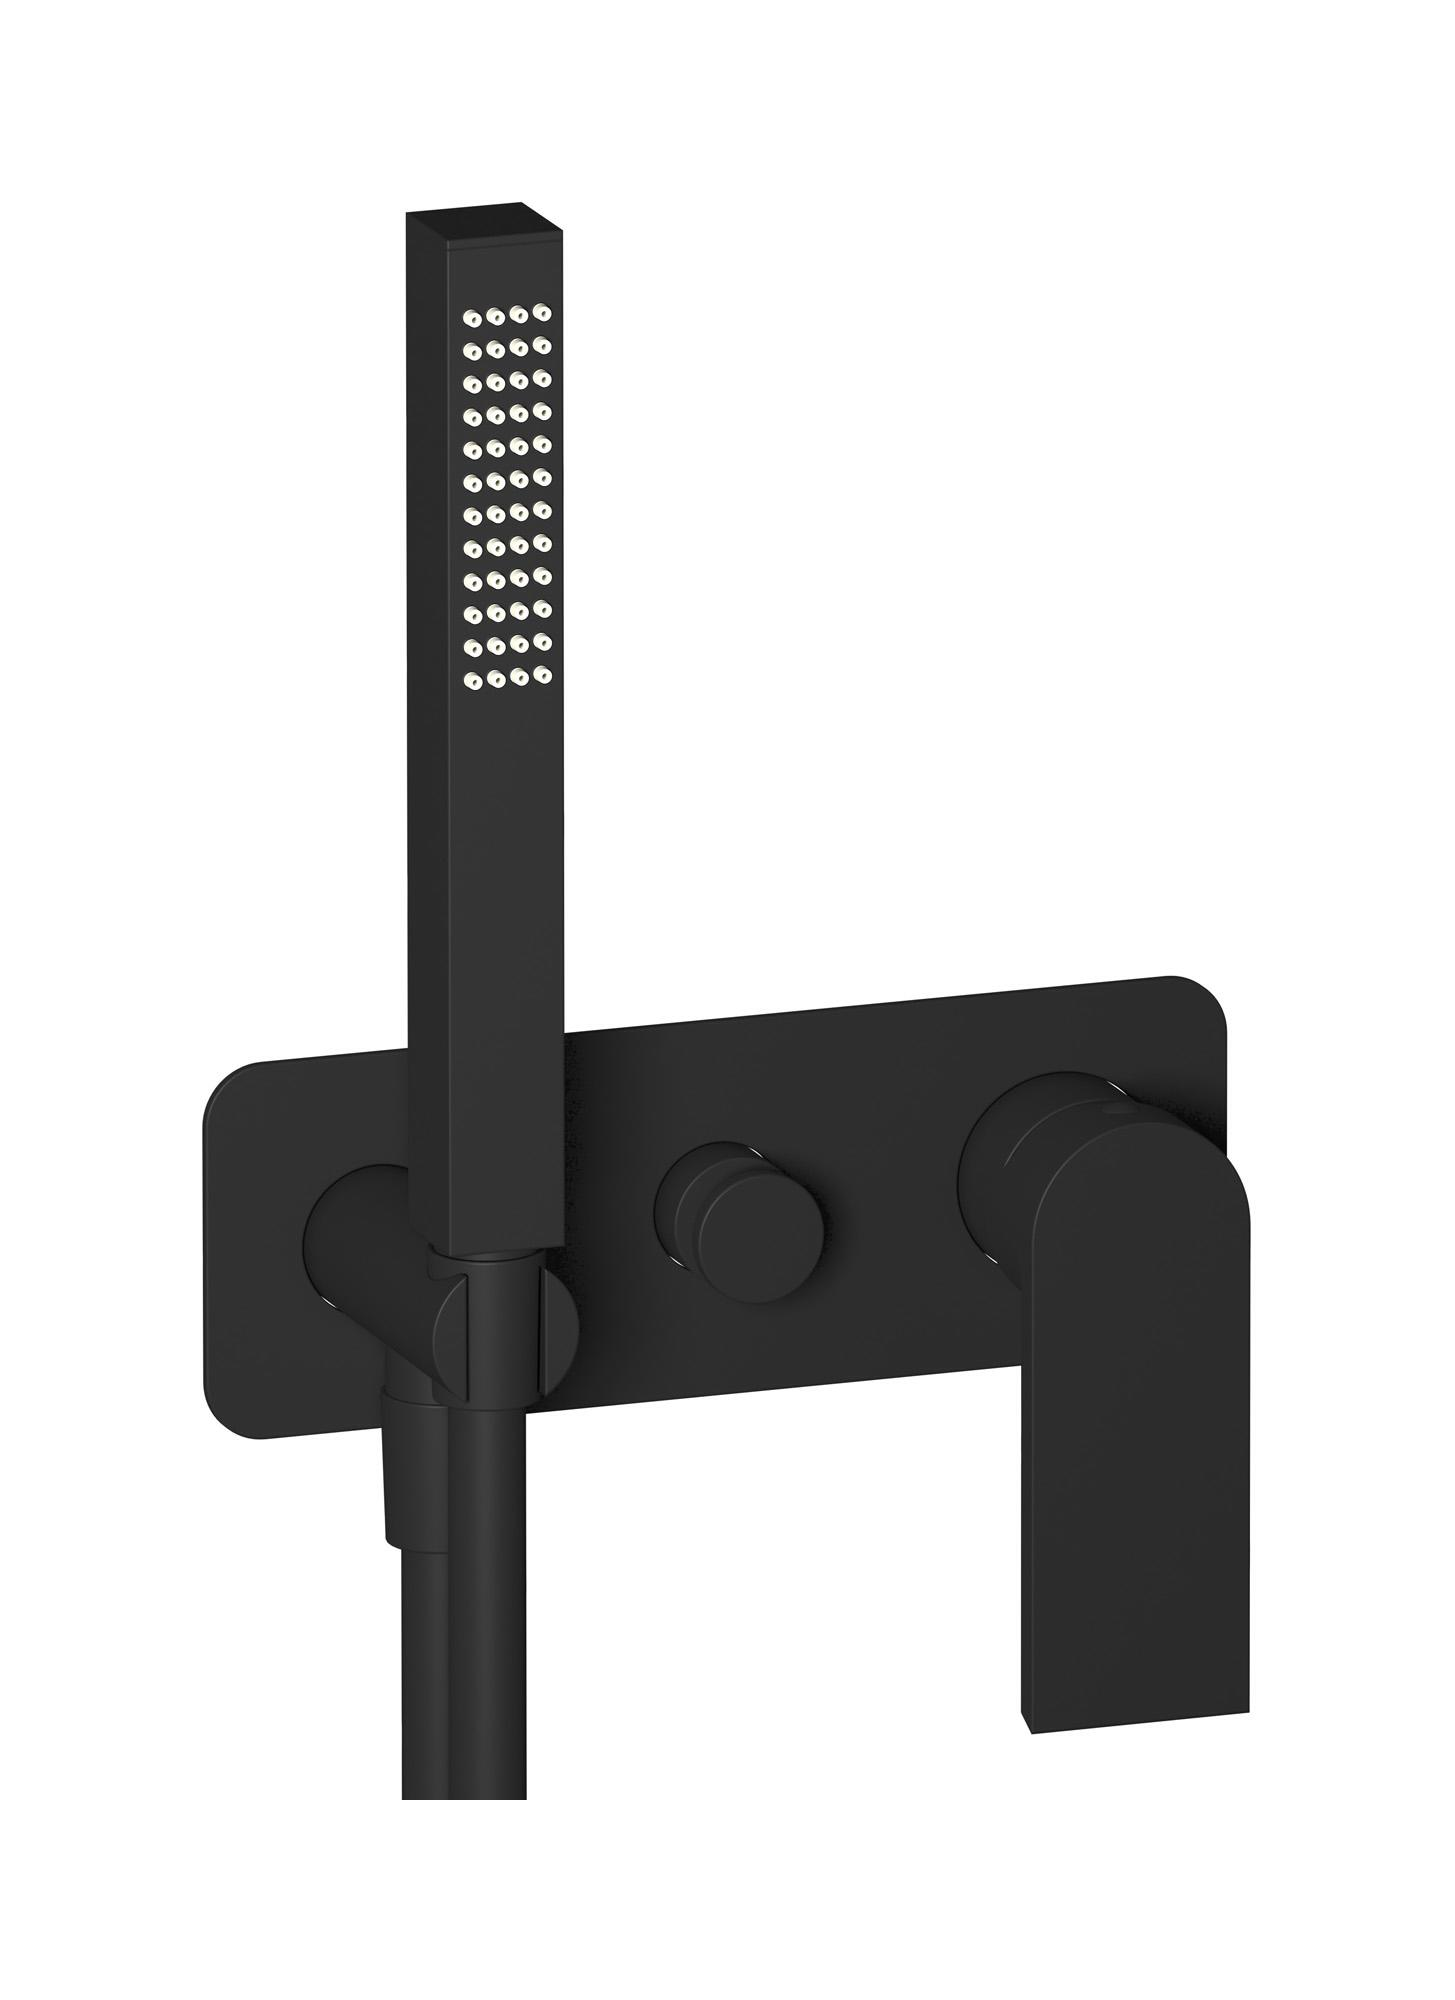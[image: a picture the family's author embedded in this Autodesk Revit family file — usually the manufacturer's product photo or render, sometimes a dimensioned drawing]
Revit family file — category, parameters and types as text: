
# Revit family: K3313
name_source: partatom
category: Apparecchi idraulici
units: mm (PartAtom-declared; Revit-internal decimal feet)

## family parameters
Basato su piano di lavoro = No
Condiviso = No
Mantieni orientamento annotazione = No
Numero OmniClass = 23.45.55.17
Punto di calcolo locali = No
Quota connettore circolare = Usa diametro
Sempre verticale = Sì
Taglio con vuoti quando caricato = No
Tipo di parte = Normale
Titolo OmniClass = Mixing Faucets

## types (8) — shared parameters
Cold water inlet = 10 mm  [stored 0.0328084 ft]
Commenti sul tipo = Wall mixer
Connessione CW = No
Connessione HW = No
Connessione di scarico = No
Connessione di ventilazione = No
Descrizione = Exposed parts for manual wall mixer with two ways diverter and shower kit
Hot water inlet = 10 mm  [stored 0.0328084 ft]
Produttore = IB Rubinetterie S.p.A.
URL = https://www.weareib.it
zero-valued in all types: Prospetto di default

## per-type parameters (varying)
| type | Finishes surface | Immagine tipo | Modello |
| Chrome | IB_Chrome | K3313CC.jpg | K3313CC |
| Brushed nickel | IB_Brushed nickel | K3313SS.jpg | K3313SS |
| Matt black | IB_matt black | K3313NP.jpg | K3313NP |
| Matt white | IB_matt white | K3313BO.jpg | K3313BO |
| Pale gold | IB_Pale gold | K3313II.jpg | K3313II |
| Brushed pale gold | IB_brushed pale gold | K3313IS.jpg | K3313IS |
| Rose gold | IB_Rose gold | K3313RS.jpg | K3313RS |
| Gold | IB_gold | K3313OO.jpg | K3313OO |

note: [stored X ft] marks values corroborated as IEEE doubles in the binary element streams (Revit-internal decimal feet)
